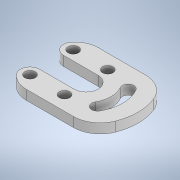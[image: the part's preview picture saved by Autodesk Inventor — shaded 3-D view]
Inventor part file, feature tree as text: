
AUTODESK INVENTOR PART (.ipt)
format: ipt  version: 2021 (Build 250183000, 183)  size: 160,256 bytes
history: native  units: mm
features: extrude x1, sketch x1
ambient origin geometry x8: Origin, YZ Plane, XZ Plane, XY Plane, X Axis, Y Axis, Z Axis, Center Point
bodies: Solid1 (feature_tree)
feature tree (2):
  extrude  "Extrusion1"  Depth=75.0mm
  sketch  "Sketch1"  dims[d0=108.0mm d1=75.0mm d4=25.0mm d5=11.0mm d6=11.0mm d7=45.0mm d8=22.5mm d9=37.5mm d10=37.5mm d11=56.0mm d12=64.0mm d13=30.0deg d14=30.0deg d15=12.0mm d16=12.0mm d17=20.0mm d18=20.0mm d19=36.0mm d20=36.0mm d21=50.0mm d22=50.0mm d23=11.0mm d24=11.0mm d25=10.0mm d26=0.0mm]
